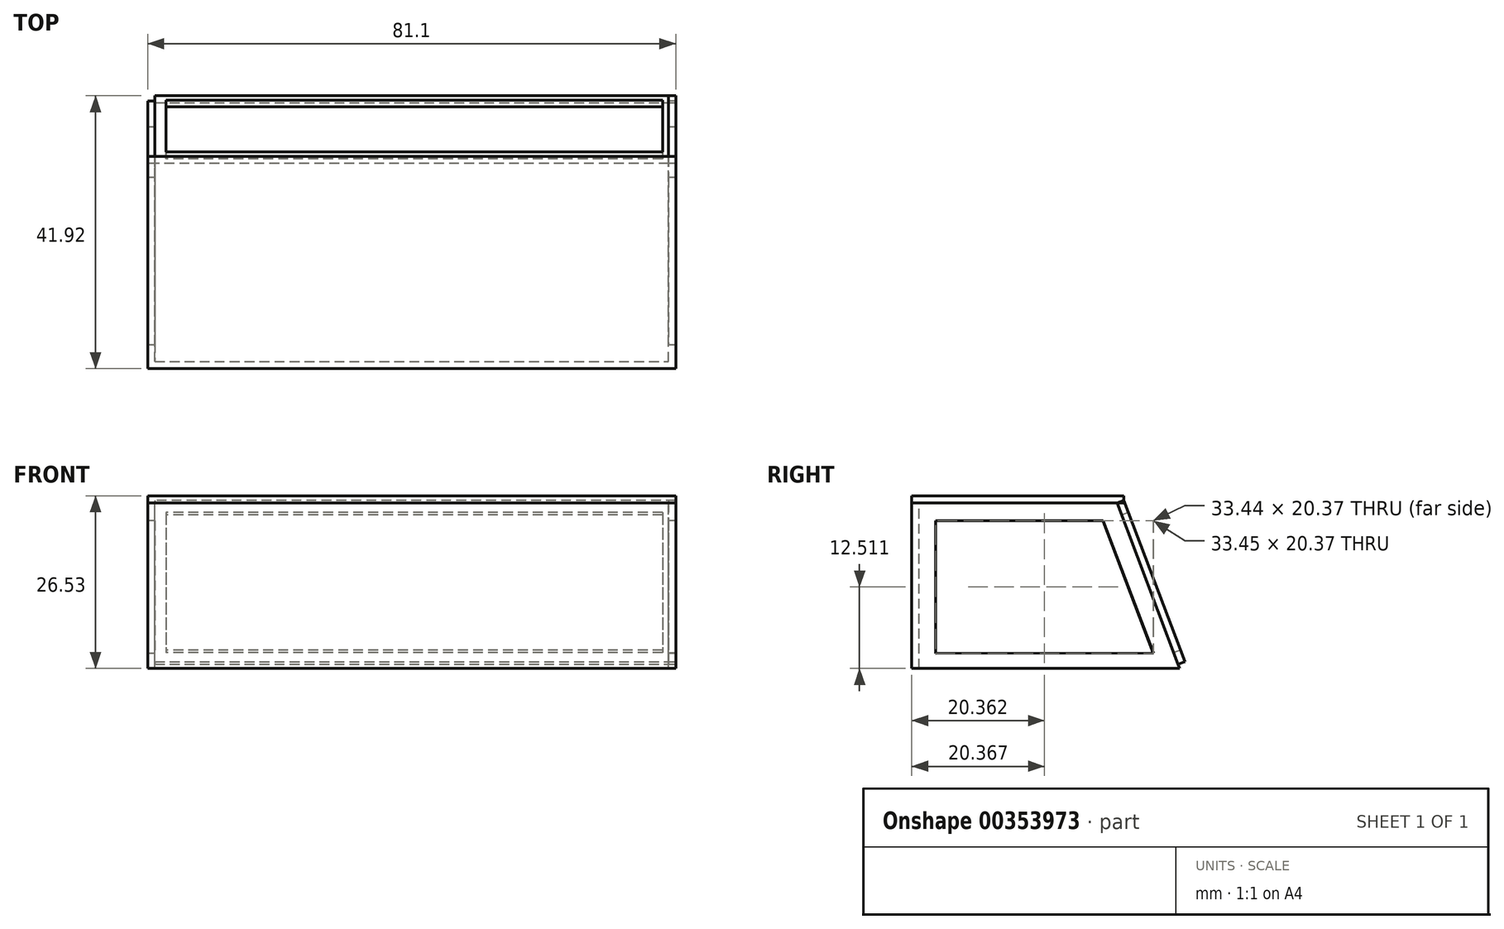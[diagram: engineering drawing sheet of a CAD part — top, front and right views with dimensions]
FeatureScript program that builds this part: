
annotation { "Feature Type Name" : "Feature", "Feature Type Description" : "" }
export const myFeature = defineFeature(function(context is Context, id is Id, definition is map)
    precondition{}
    {
        {
            var Q0;
            Q0=qCreatedBy(makeId("Right.planeOp"),FACE);
            var sketch = newSketch(context, id + "F0", { "sketchPlane" : qUnion([Q0])});
            skLineSegment(sketch, "E0", {"start": v(-20, 0) * mm, "end": v(-20, 25.43) * mm});
            skLineSegment(sketch, "E1", {"start": v(20, 0) * mm, "end": v(10.45, 25.43) * mm});
            skLineSegment(sketch, "E2", {"start": v(10.45, 25.43) * mm, "end": v(-20, 25.43) * mm});
            skLineSegment(sketch, "E3", {"start": v(-20, 0) * mm, "end": v(20, 0) * mm});
            skLineSegment(sketch, "E4", {"start": v(15.98, 2.33) * mm, "end": v(-17.46, 2.33) * mm});
            skLineSegment(sketch, "E5", {"start": v(-17.46, 2.33) * mm, "end": v(-17.46, 22.7) * mm});
            skLineSegment(sketch, "E6", {"start": v(-17.46, 22.7) * mm, "end": v(8.25, 22.7) * mm});
            skLineSegment(sketch, "E7", {"start": v(8.25, 22.7) * mm, "end": v(15.98, 2.33) * mm});
            skLineSegment(sketch, "E8.bottom", {"start": v(-20, 0) * mm, "end": v(0, 0) * mm});
            skPoint(sketch, "E9.firstSnap0", {"position": v(-0.74, 2.33) * mm});
            skLineSegment(sketch, "E9.bottom", {"start": v(-0.74, 0) * mm, "end": v(-21.23, 0) * mm});
            skSolve(sketch);
        }
        {
            var Q0;
            Q0=makeQuery(id+"F0.imprint","IMPRINT",FACE,{"disambiguationData":[TD([[makeQuery(id+"F0.imprint","IMPRINT",EDGE,{"derivedFrom":sQuery(id+"F0.wireOp",EDGE,"E0")}),-1.0]])]});
            var Q1;
            Q1=makeQuery(id+"F0.imprint","IMPRINT",FACE,{"disambiguationData":[TD([[makeQuery(id+"F0.imprint","IMPRINT",EDGE,{"derivedFrom":sQuery(id+"F0.wireOp",EDGE,"E8.bottom")}),-1.0]])]});
            var Q2;
            Q2=makeQuery(id+"F0.imprint","IMPRINT",FACE,{"disambiguationData":[TD([[makeQuery(id+"F0.imprint","IMPRINT",EDGE,{"derivedFrom":sQuery(id+"F0.wireOp",EDGE,"E9.top")}),-1.0]])]});
            var Q3;
            Q3=makeQuery(id+"F0.imprint","IMPRINT",FACE,{"disambiguationData":[TD([[makeQuery(id+"F0.imprint","IMPRINT",EDGE,{"derivedFrom":sQuery(id+"F0.wireOp",EDGE,"quDWu2sP-DqDO-X9ur-Zvbd-zb49WhtbQRHx.top")}),1.0]])]});
            extrude(context, id + "F1", {"entities" : qUnion([Q0, Q1, Q2, Q3]), "endBound" : BoundingType.SYMMETRIC, "depth" : 1.1 * mm});
        }
        {
            var Q0;
            Q0=makeQuery(id+"F1.opExtrude","SWEPT_FACE",FACE,{"disambiguationData":[OSD([sQuery(id+"F0.wireOp",EDGE,"E0")])]});
            var sketch = newSketch(context, id + "F2", { "sketchPlane" : qUnion([Q0])});
            skLineSegment(sketch, "E10.bottom", {"start": v(-0.55, 25.43) * mm, "end": v(79.45, 25.43) * mm});
            skLineSegment(sketch, "E10.top", {"start": v(-0.55, 0) * mm, "end": v(79.45, 0) * mm});
            skLineSegment(sketch, "E10.left", {"start": v(-0.55, 25.43) * mm, "end": v(-0.55, 0) * mm});
            skLineSegment(sketch, "E10.right", {"start": v(79.45, 25.43) * mm, "end": v(79.45, 0) * mm});
            skSolve(sketch);
        }
        {
            var Q0;
            {var subQ2=sQuery(id+"F2.wireOp",EDGE,"E10.right");Q0=makeQuery(id+"F2.imprint","IMPRINT",FACE,{"disambiguationData":[TD([[makeQuery(id+"F2.imprint","IMPRINT",EDGE,{"derivedFrom":subQ2}),-1.0]])]});}
            var Q1;
            {var subQ0=sQuery(id+"F2.wireOp",EDGE,"E10.left");Q1=makeQuery(id+"F2.imprint","IMPRINT",FACE,{"disambiguationData":[TD([[makeQuery(id+"F2.imprint","IMPRINT",EDGE,{"derivedFrom":subQ0}),-1.0]])]});}
            extrude(context, id + "F3", {"entities" : qUnion([Q0, Q1]), "operationType" : NewBodyOperationType.ADD, "depth" : 1.1 * mm});
        }
        {
            var Q0;
            Q0=makeQuery(id+"F3.opExtrude","SWEPT_FACE",FACE,{"disambiguationData":[OSD([sQuery(id+"F2.wireOp",EDGE,"E10.right")])]});
            var sketch = newSketch(context, id + "F4", { "sketchPlane" : qUnion([Q0])});
            skLineSegment(sketch, "E11", {"start": v(-21.1, 0) * mm, "end": v(20.03, 0) * mm});
            skLineSegment(sketch, "E12", {"start": v(20.03, 0) * mm, "end": v(10.45, 25.43) * mm});
            skLineSegment(sketch, "E13", {"start": v(-21.1, 25.43) * mm, "end": v(10.45, 25.43) * mm});
            skLineSegment(sketch, "E14", {"start": v(16, 2.36) * mm, "end": v(8.25, 22.7) * mm});
            skLineSegment(sketch, "E15", {"start": v(8.25, 22.7) * mm, "end": v(-17.46, 22.7) * mm});
            skLineSegment(sketch, "E16", {"start": v(-17.46, 22.7) * mm, "end": v(-17.46, 2.33) * mm});
            skLineSegment(sketch, "E17", {"start": v(-17.46, 2.33) * mm, "end": v(16, 2.36) * mm});
            skLineSegment(sketch, "E18.bottom", {"start": v(-21.1, 0) * mm, "end": v(20.08, 0) * mm});
            skLineSegment(sketch, "E19.bottom", {"start": v(-21.1, 0) * mm, "end": v(0, 0) * mm});
            skSolve(sketch);
        }
        {
            var Q0;
            {var subQ2=sQuery(id+"F4.wireOp",EDGE,"E12");Q0=makeQuery(id+"F4.imprint","IMPRINT",FACE,{"disambiguationData":[TD([[makeQuery(id+"F4.imprint","IMPRINT",EDGE,{"derivedFrom":subQ2}),1.0]])]});}
            var Q1;
            {var subQ1=sQuery(id+"F2.wireOp",EDGE,"E10.right");var subQ2=makeQuery(id+"F3.opExtrude","CAP_EDGE",EDGE,{"disambiguationData":[OSD([subQ1])],"isStart":true});Q1=makeQuery(id+"F4.imprint","IMPRINT",FACE,{"disambiguationData":[TD([[makeQuery(id+"F4.imprint","IMPRINT",EDGE,{"derivedFrom":subQ2}),-1.0]])]});}
            var Q2;
            Q2=makeQuery(id+"F4.imprint","IMPRINT",FACE,{"disambiguationData":[TD([[makeQuery(id+"F4.imprint","IMPRINT",EDGE,{"derivedFrom":sQuery(id+"F4.wireOp",EDGE,"E18.top")}),1.0]])]});
            var Q3;
            Q3=makeQuery(id+"F4.imprint","IMPRINT",FACE,{"disambiguationData":[TD([[makeQuery(id+"F4.imprint","IMPRINT",EDGE,{"derivedFrom":sQuery(id+"F4.wireOp",EDGE,"E19.top")}),1.0]])]});
            extrude(context, id + "F5", {"entities" : qUnion([Q0, Q1, Q2, Q3]), "operationType" : NewBodyOperationType.ADD, "depth" : 1.1 * mm});
        }
        {
            var Q0;
            Q0=makeQuery(id+"F5.opExtrude","SWEPT_FACE",FACE,{"disambiguationData":[OSD([sQuery(id+"F4.wireOp",EDGE,"E12")])]});
            var sketch = newSketch(context, id + "F6", { "sketchPlane" : qUnion([Q0])});
            skLineSegment(sketch, "E20.bottom", {"start": v(-0.55, -6.39) * mm, "end": v(-80.55, -6.39) * mm});
            skLineSegment(sketch, "E20.top", {"start": v(-0.55, 20.11) * mm, "end": v(-80.55, 20.11) * mm});
            skLineSegment(sketch, "E20.left", {"start": v(-0.55, -6.39) * mm, "end": v(-0.55, 20.11) * mm});
            skLineSegment(sketch, "E20.right", {"start": v(-80.55, -6.39) * mm, "end": v(-80.55, 20.11) * mm});
            skLineSegment(sketch, "E21.bottom", {"start": v(-78.52, 18.1) * mm, "end": v(-2.29, 18.1) * mm});
            skLineSegment(sketch, "E21.top", {"start": v(-78.52, -4.45) * mm, "end": v(-2.29, -4.45) * mm});
            skLineSegment(sketch, "E21.left", {"start": v(-78.52, 18.1) * mm, "end": v(-78.52, -4.45) * mm});
            skLineSegment(sketch, "E21.right", {"start": v(-2.29, 18.1) * mm, "end": v(-2.29, -4.45) * mm});
            skSolve(sketch);
        }
        {
            var Q0;
            Q0=makeQuery(id+"F6.imprint","IMPRINT",FACE,{"disambiguationData":[TD([[makeQuery(id+"F6.imprint","IMPRINT",EDGE,{"derivedFrom":sQuery(id+"F6.wireOp",EDGE,"E20.bottom")}),-1.0]])]});
            var Q1;
            {var subQ0=sQuery(id+"F6.wireOp",EDGE,"E20.left");Q1=makeQuery(id+"F6.imprint","IMPRINT",FACE,{"disambiguationData":[TD([[makeQuery(id+"F6.imprint","IMPRINT",EDGE,{"derivedFrom":subQ0}),1.0]])]});}
            extrude(context, id + "F7", {"entities" : qUnion([Q0, Q1]), "operationType" : NewBodyOperationType.ADD, "depth" : 1.1 * mm});
        }
        {
            var Q0;
            {var subQ3=sQuery(id+"F6.wireOp",EDGE,"E20.right");Q0=makeQuery(id+"F6.imprint","IMPRINT",FACE,{"disambiguationData":[TD([[makeQuery(id+"F6.imprint","IMPRINT",EDGE,{"derivedFrom":subQ3}),-1.0]])]});}
            var Q1;
            Q1=makeQuery(id+"F6.imprint","IMPRINT",FACE,{"disambiguationData":[TD([[makeQuery(id+"F6.imprint","IMPRINT",EDGE,{"derivedFrom":sQuery(id+"F6.wireOp",EDGE,"E20.bottom")}),-1.0]])]});
            extrude(context, id + "F8", {"entities" : qUnion([Q0, Q1]), "depth" : 1.1 * mm});
        }
        {
            var Q0;
            {var subQ0=sQuery(id+"F4.wireOp",EDGE,"E13");var subQ1=sQuery(id+"F2.wireOp",EDGE,"E10.right");Q0=makeQuery(id+"F5.boolean.opBoolean","MERGE",FACE,{"derivedFrom":[makeQuery(id+"F3.boolean.opBoolean","MERGE",FACE,{"derivedFrom":[makeQuery(id+"F1.opExtrude","SWEPT_FACE",FACE,{"disambiguationData":[OSD([sQuery(id+"F0.wireOp",EDGE,"E2")])]}),makeQuery(id+"F3.opExtrude","SWEPT_FACE",FACE,{"disambiguationData":[OSD([sQuery(id+"F2.wireOp",EDGE,"E10.bottom")])]})]}),makeQuery(id+"F5.opExtrude","SWEPT_FACE",FACE,{"disambiguationData":[OSD([subQ0]),TDD([makeQuery(id+"F4.imprint","IMPRINT",EDGE,{"disambiguationData":[TD([[makeQuery(id+"F4.imprint","INTERSECT",VERTEX,{"derivedFrom":[makeQuery(id+"F3.opExtrude","CAP_EDGE",EDGE,{"disambiguationData":[OSD([subQ1])],"isStart":true}),subQ0]}),1.0]])],"derivedFrom":subQ0})])]})]});}
            var sketch = newSketch(context, id + "F9", { "sketchPlane" : qUnion([Q0])});
            skLineSegment(sketch, "E22.bottom", {"start": v(80.55, -21.1) * mm, "end": v(-0.55, -21.1) * mm});
            skLineSegment(sketch, "E22.top", {"start": v(80.55, 11.47) * mm, "end": v(-0.55, 11.47) * mm});
            skLineSegment(sketch, "E22.left", {"start": v(80.55, -21.1) * mm, "end": v(80.55, 11.47) * mm});
            skLineSegment(sketch, "E22.right", {"start": v(-0.55, -21.1) * mm, "end": v(-0.55, 11.47) * mm});
            skSolve(sketch);
        }
        {
            var Q0;
            {var subQ3=sQuery(id+"F9.wireOp",EDGE,"E22.top");Q0=makeQuery(id+"F9.imprint","IMPRINT",FACE,{"disambiguationData":[TD([[makeQuery(id+"F9.imprint","IMPRINT",EDGE,{"derivedFrom":subQ3}),1.0]])]});}
            var Q1;
            {var subQ3=sQuery(id+"F9.wireOp",EDGE,"E22.bottom");Q1=makeQuery(id+"F9.imprint","IMPRINT",FACE,{"disambiguationData":[TD([[makeQuery(id+"F9.imprint","IMPRINT",EDGE,{"derivedFrom":subQ3}),1.0]])]});}
            extrude(context, id + "F10", {"entities" : qUnion([Q0, Q1]), "depth" : 1.1 * mm});
        }
    });
